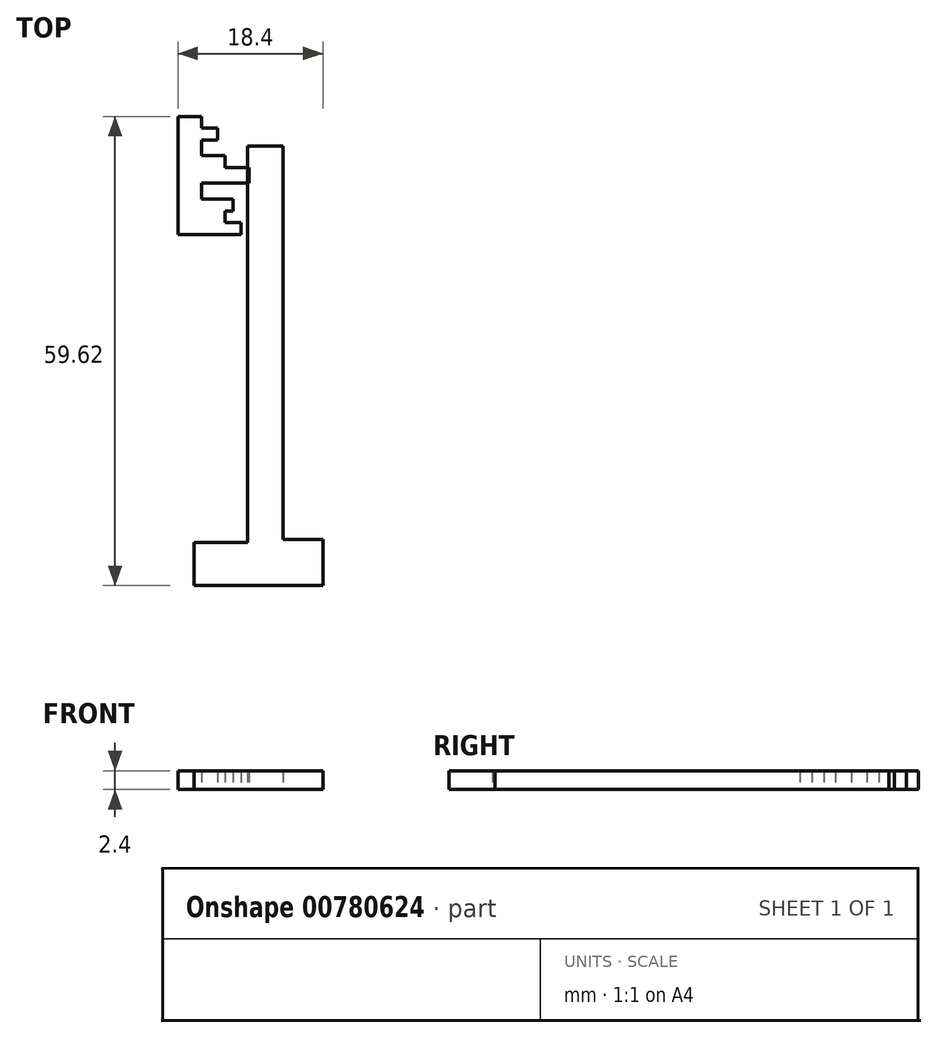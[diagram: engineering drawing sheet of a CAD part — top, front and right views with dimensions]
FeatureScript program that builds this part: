
annotation { "Feature Type Name" : "Feature", "Feature Type Description" : "" }
export const myFeature = defineFeature(function(context is Context, id is Id, definition is map)
    precondition{}
    {
        {
            var Q0;
            Q0=qCreatedBy(makeId("Top.planeOp"),FACE);
            var sketch = newSketch(context, id + "F0", { "sketchPlane" : qUnion([Q0])});
            skLineSegment(sketch, "E0", {"start": v(-31.72, 38.97) * mm, "end": v(-28.72, 38.97) * mm});
            skLineSegment(sketch, "E1", {"start": v(-28.72, 38.97) * mm, "end": v(-28.72, 37.47) * mm});
            skLineSegment(sketch, "E2", {"start": v(-28.72, 37.47) * mm, "end": v(-26.72, 37.47) * mm});
            skLineSegment(sketch, "E3", {"start": v(-26.72, 37.47) * mm, "end": v(-26.72, 35.97) * mm});
            skLineSegment(sketch, "E4", {"start": v(-26.72, 35.97) * mm, "end": v(-28.72, 35.97) * mm});
            skLineSegment(sketch, "E5", {"start": v(-28.72, 35.97) * mm, "end": v(-28.72, 33.97) * mm});
            skLineSegment(sketch, "E6", {"start": v(-28.72, 33.97) * mm, "end": v(-25.72, 33.97) * mm});
            skLineSegment(sketch, "E7", {"start": v(-25.72, 33.97) * mm, "end": v(-25.72, 32.47) * mm});
            skLineSegment(sketch, "E8", {"start": v(-25.72, 32.47) * mm, "end": v(-22.72, 32.47) * mm});
            skLineSegment(sketch, "E9", {"start": v(-22.72, 32.47) * mm, "end": v(-22.72, 30.47) * mm});
            skLineSegment(sketch, "E10", {"start": v(-22.72, 30.47) * mm, "end": v(-28.72, 30.47) * mm});
            skLineSegment(sketch, "E11", {"start": v(-28.72, 30.47) * mm, "end": v(-28.72, 28.47) * mm});
            skLineSegment(sketch, "E12", {"start": v(-28.72, 28.47) * mm, "end": v(-24.72, 28.47) * mm});
            skLineSegment(sketch, "E13", {"start": v(-24.72, 28.47) * mm, "end": v(-24.72, 26.97) * mm});
            skLineSegment(sketch, "E14", {"start": v(-24.72, 26.97) * mm, "end": v(-25.72, 26.97) * mm});
            skLineSegment(sketch, "E15", {"start": v(-25.72, 26.97) * mm, "end": v(-25.72, 25.47) * mm});
            skLineSegment(sketch, "E16", {"start": v(-25.72, 25.47) * mm, "end": v(-23.72, 25.47) * mm});
            skLineSegment(sketch, "E17", {"start": v(-23.72, 25.47) * mm, "end": v(-23.72, 23.97) * mm});
            skLineSegment(sketch, "E18", {"start": v(-23.72, 23.97) * mm, "end": v(-31.72, 23.97) * mm});
            skLineSegment(sketch, "E19", {"start": v(-31.72, 38.97) * mm, "end": v(-31.72, 37.47) * mm});
            skLineSegment(sketch, "E20", {"start": v(-31.72, 35.97) * mm, "end": v(-31.72, 37.47) * mm});
            skLineSegment(sketch, "E21", {"start": v(-31.72, 35.97) * mm, "end": v(-31.72, 33.97) * mm});
            skLineSegment(sketch, "E22", {"start": v(-31.72, 32.47) * mm, "end": v(-31.72, 38.97) * mm});
            skLineSegment(sketch, "E23", {"start": v(-31.72, 23.97) * mm, "end": v(-31.72, 38.97) * mm});
            skLineSegment(sketch, "E24", {"start": v(-3.12, 6.93) * mm, "end": v(-0.12, 6.93) * mm});
            skLineSegment(sketch, "E25", {"start": v(-0.12, 6.93) * mm, "end": v(-0.12, 5.43) * mm});
            skLineSegment(sketch, "E26", {"start": v(-0.12, 5.43) * mm, "end": v(-3.12, 5.43) * mm});
            skLineSegment(sketch, "E27", {"start": v(-3.12, 5.43) * mm, "end": v(1.88, 5.43) * mm});
            skLineSegment(sketch, "E28", {"start": v(1.88, 5.43) * mm, "end": v(1.88, 3.93) * mm});
            skLineSegment(sketch, "E29", {"start": v(1.88, 3.93) * mm, "end": v(-3.12, 3.93) * mm});
            skLineSegment(sketch, "E30", {"start": v(-3.12, 3.93) * mm, "end": v(-0.12, 3.93) * mm});
            skLineSegment(sketch, "E31", {"start": v(-0.12, 3.93) * mm, "end": v(-0.12, 1.93) * mm});
            skLineSegment(sketch, "E32", {"start": v(-0.12, 1.93) * mm, "end": v(-3.12, 1.93) * mm});
            skLineSegment(sketch, "E33", {"start": v(-3.12, 1.93) * mm, "end": v(2.88, 1.93) * mm});
            skLineSegment(sketch, "E34", {"start": v(2.88, 1.93) * mm, "end": v(2.88, 0.43) * mm});
            skLineSegment(sketch, "E35", {"start": v(2.88, 0.43) * mm, "end": v(-3.12, 0.43) * mm});
            skLineSegment(sketch, "E36", {"start": v(-3.12, 0.43) * mm, "end": v(5.88, 0.43) * mm});
            skLineSegment(sketch, "E37", {"start": v(5.88, 0.43) * mm, "end": v(5.88, -1.57) * mm});
            skLineSegment(sketch, "E38", {"start": v(5.88, -1.57) * mm, "end": v(-3.12, -1.57) * mm});
            skLineSegment(sketch, "E39", {"start": v(-3.12, -1.57) * mm, "end": v(-0.12, -1.57) * mm});
            skLineSegment(sketch, "E40", {"start": v(-0.12, -1.57) * mm, "end": v(-0.12, -3.57) * mm});
            skLineSegment(sketch, "E41", {"start": v(-0.12, -3.57) * mm, "end": v(-3.12, -3.57) * mm});
            skLineSegment(sketch, "E42", {"start": v(-3.12, -3.57) * mm, "end": v(3.88, -3.57) * mm});
            skLineSegment(sketch, "E43", {"start": v(3.88, -3.57) * mm, "end": v(3.88, -5.07) * mm});
            skLineSegment(sketch, "E44", {"start": v(3.88, -5.07) * mm, "end": v(-3.12, -5.07) * mm});
            skLineSegment(sketch, "E45", {"start": v(-3.12, -5.07) * mm, "end": v(2.88, -5.07) * mm});
            skLineSegment(sketch, "E46", {"start": v(2.88, -5.07) * mm, "end": v(2.88, -6.57) * mm});
            skLineSegment(sketch, "E47", {"start": v(2.88, -6.57) * mm, "end": v(-3.12, -6.57) * mm});
            skLineSegment(sketch, "E48", {"start": v(-3.12, -6.57) * mm, "end": v(4.88, -6.57) * mm});
            skLineSegment(sketch, "E49", {"start": v(4.88, -6.57) * mm, "end": v(4.88, -8.07) * mm});
            skLineSegment(sketch, "E50", {"start": v(4.88, -8.07) * mm, "end": v(-3.12, -8.07) * mm});
            skLineSegment(sketch, "E51", {"start": v(-3.12, 6.93) * mm, "end": v(-3.12, 5.43) * mm});
            skLineSegment(sketch, "E52", {"start": v(-3.12, 3.93) * mm, "end": v(-3.12, 5.43) * mm});
            skLineSegment(sketch, "E53", {"start": v(-3.12, 3.93) * mm, "end": v(-3.12, 1.93) * mm});
            skLineSegment(sketch, "E54", {"start": v(-3.12, 0.43) * mm, "end": v(-3.12, 6.93) * mm});
            skLineSegment(sketch, "E55", {"start": v(-3.12, -8.07) * mm, "end": v(-3.12, 6.93) * mm});
            skPoint(sketch, "E56.orphan", {"position": v(-31.72, 30.47) * mm});
            skPoint(sketch, "E57.orphan", {"position": v(-31.72, 28.47) * mm});
            skPoint(sketch, "E58.orphan", {"position": v(-31.72, 26.97) * mm});
            skPoint(sketch, "E59.end.orphan", {"position": v(-31.72, 25.47) * mm});
            skSolve(sketch);
        }
        {
            var Q0;
            {var subQ0=sQuery(id+"F0.wireOp",EDGE,"E0");Q0=makeQuery(id+"F0.imprint","IMPRINT",FACE,{"disambiguationData":[TD([[makeQuery(id+"F0.imprint","IMPRINT",EDGE,{"derivedFrom":subQ0}),-1.0]])]});}
            extrude(context, id + "F1", {"entities" : qUnion([Q0]), "depth" : 2.4 * mm, "offsetDistance" : 25 * mm});
        }
        {
            var Q0;
            Q0=qCreatedBy(makeId("Top.planeOp"),FACE);
            var sketch = newSketch(context, id + "F2", { "sketchPlane" : qUnion([Q0])});
            skLineSegment(sketch, "E60", {"start": v(-22.9, 35.23) * mm, "end": v(-18.4, 35.23) * mm});
            skLineSegment(sketch, "E61", {"start": v(-18.4, 35.23) * mm, "end": v(-18.4, -14.77) * mm});
            skLineSegment(sketch, "E62", {"start": v(-18.4, -14.77) * mm, "end": v(-13.32, -14.77) * mm});
            skLineSegment(sketch, "E63", {"start": v(-13.32, -14.77) * mm, "end": v(-13.32, -20.65) * mm});
            skLineSegment(sketch, "E64", {"start": v(-13.32, -20.65) * mm, "end": v(-29.68, -20.65) * mm});
            skLineSegment(sketch, "E65", {"start": v(-29.68, -20.65) * mm, "end": v(-29.68, -15.14) * mm});
            skLineSegment(sketch, "E66", {"start": v(-29.68, -15.14) * mm, "end": v(-22.9, -15.14) * mm});
            skLineSegment(sketch, "E67", {"start": v(-22.9, -15.14) * mm, "end": v(-22.9, 35.23) * mm});
            skSolve(sketch);
        }
        {
            var Q0;
            Q0=makeQuery(id+"F2.imprint","IMPRINT",FACE,{"disambiguationData":[TD([[makeQuery(id+"F2.imprint","IMPRINT",EDGE,{"derivedFrom":sQuery(id+"F2.wireOp",EDGE,"E60")}),-1.0]])]});
            extrude(context, id + "F3", {"entities" : qUnion([Q0]), "depth" : 2.4 * mm, "offsetDistance" : 25 * mm});
        }
    });
